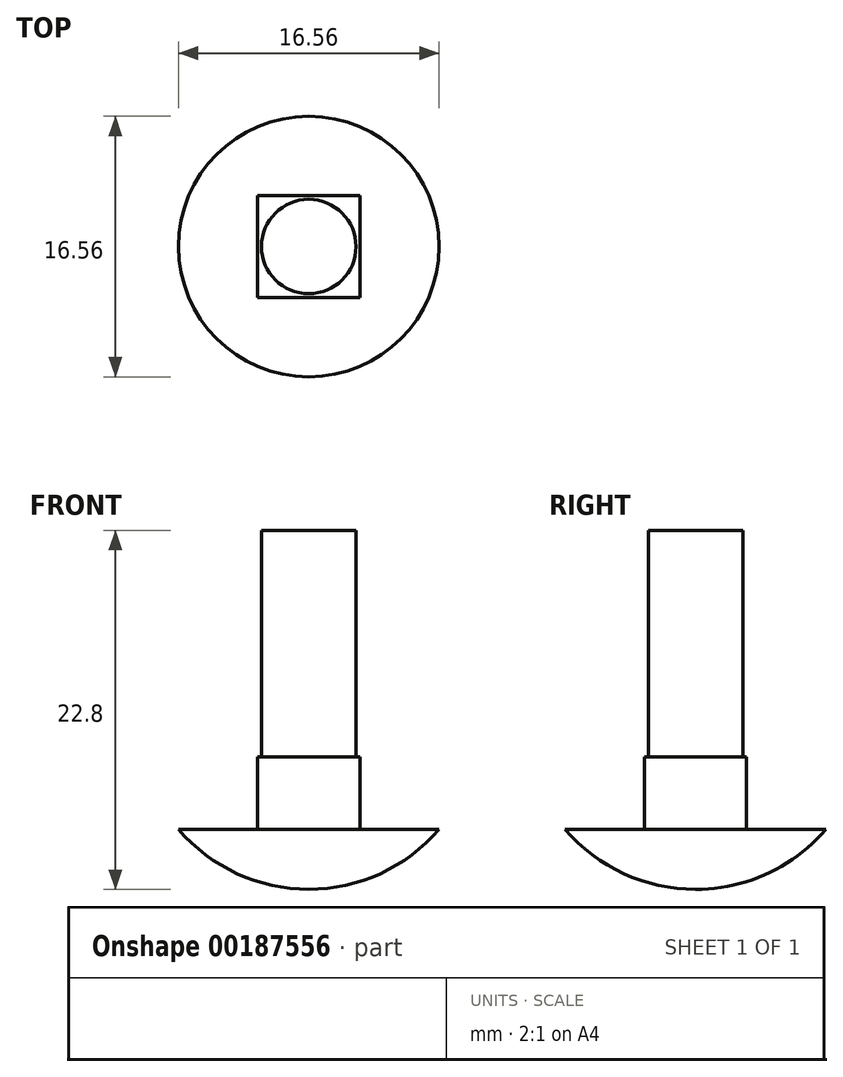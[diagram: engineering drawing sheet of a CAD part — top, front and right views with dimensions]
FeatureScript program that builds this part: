
annotation { "Feature Type Name" : "Feature", "Feature Type Description" : "" }
export const myFeature = defineFeature(function(context is Context, id is Id, definition is map)
    precondition{}
    {
        {
            var Q0;
            Q0=qCreatedBy(makeId("Top.planeOp"),FACE);
            var sketch = newSketch(context, id + "F0", { "sketchPlane" : qUnion([Q0])});
            skLineSegment(sketch, "E0.bottom", {"start": v(3.25, 3.25) * mm, "end": v(-3.25, 3.25) * mm});
            skLineSegment(sketch, "E0.top", {"start": v(3.25, -3.25) * mm, "end": v(-3.25, -3.25) * mm});
            skLineSegment(sketch, "E0.left", {"start": v(3.25, 3.25) * mm, "end": v(3.25, -3.25) * mm});
            skLineSegment(sketch, "E0.right", {"start": v(-3.25, 3.25) * mm, "end": v(-3.25, -3.25) * mm});
            skPoint(sketch, "E0.middle", {"position": v(0, 0) * mm});
            skSolve(sketch);
        }
        {
            var Q0;
            Q0 = qSketchRegion(id + "F0", true);
            extrude(context, id + "F1", {"entities" : qUnion([Q0]), "depth" : 4.6 * mm});
        }
        {
            var Q0;
            Q0=makeQuery(id+"F1.opExtrude","CAP_FACE",FACE,{"disambiguationData":[OSD([sQuery(id+"F0.wireOp",EDGE,"E0.bottom"),sQuery(id+"F0.wireOp",EDGE,"E0.top"),sQuery(id+"F0.wireOp",EDGE,"E0.left"),sQuery(id+"F0.wireOp",EDGE,"E0.right")])],"isStart":false});
            var sketch = newSketch(context, id + "F2", { "sketchPlane" : qUnion([Q0])});
            skCircle(sketch, "E1", {"center": v(0, 0) * mm, "radius": 3 * mm});
            skSolve(sketch);
        }
        {
            var Q0;
            Q0 = qSketchRegion(id + "F2", true);
            extrude(context, id + "F3", {"entities" : qUnion([Q0]), "operationType" : NewBodyOperationType.ADD, "depth" : (19 - 4.6) * mm});
        }
        {
            var Q0;
            Q0=qCreatedBy(makeId("Right.planeOp"),FACE);
            var sketch = newSketch(context, id + "F4", { "sketchPlane" : qUnion([Q0])});
            skLineSegment(sketch, "E2", {"start": v(8.28, 0) * mm, "end": v(0, 0) * mm});
            skPoint(sketch, "E3", {"position": v(0, 0) * mm});
            skLineSegment(sketch, "E4", {"start": v(0, 0) * mm, "end": v(0, -3.8) * mm});
            skArc(sketch, "E5", {"start": v(0, -3.8) * mm, "mid": v(4.55, -2.8) * mm, "end": v(8.28, 0) * mm});
            skSolve(sketch);
        }
        {
            var Q0;
            Q0 = qSketchRegion(id + "F4", true);
            var Q1;
            Q1=sQuery(id+"F4.wireOp",EDGE,"E4");
            revolve(context, id + "F5", {"operationType" : NewBodyOperationType.ADD, "entities" : qUnion([Q0]), "axis" : qUnion([Q1]), "revolveType" : RevolveType.FULL});
        }
    });
